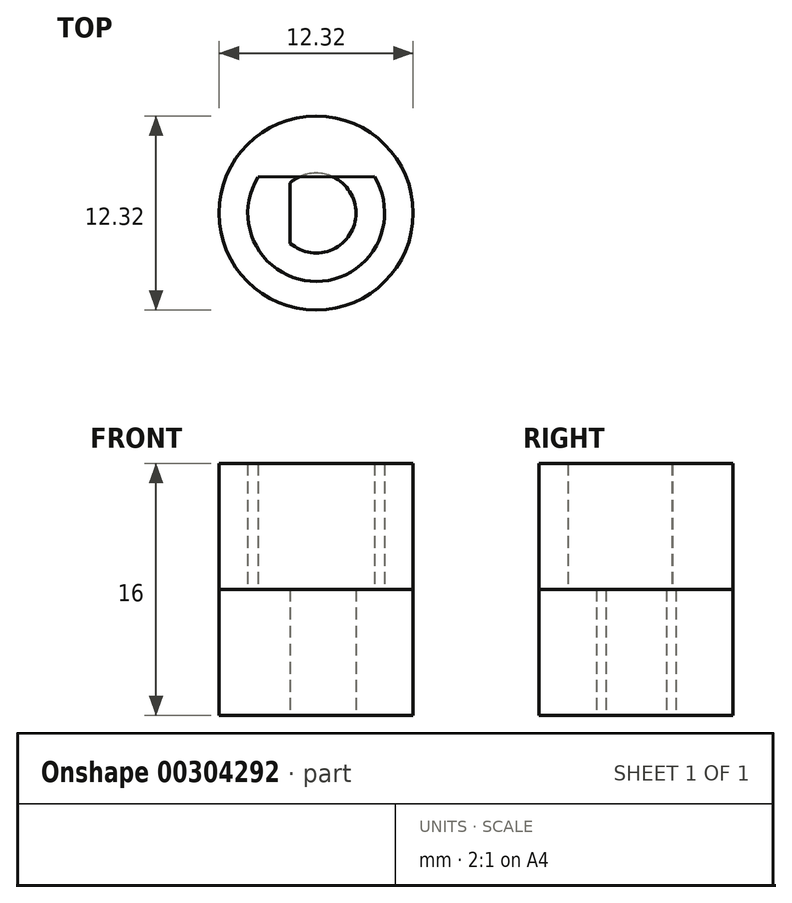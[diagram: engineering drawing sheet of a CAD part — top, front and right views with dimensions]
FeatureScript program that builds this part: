
annotation { "Feature Type Name" : "Feature", "Feature Type Description" : "" }
export const myFeature = defineFeature(function(context is Context, id is Id, definition is map)
    precondition{}
    {
        {
            var Q0;
            Q0=qCreatedBy(makeId("Top.planeOp"),FACE);
            var sketch = newSketch(context, id + "F0", { "sketchPlane" : qUnion([Q0])});
            skCircle(sketch, "E0", {"center": v(0, 0) * mm, "radius": 6.15 * mm});
            skArc(sketch, "E1.0", {"start": v(-1.65, -1.92) * mm, "mid": v(2.53, 0) * mm, "end": v(-1.65, 1.92) * mm});
            skLineSegment(sketch, "E2.0", {"start": v(-1.65, -1.92) * mm, "end": v(-1.65, 1.92) * mm});
            skSolve(sketch);
        }
        {
            var Q0;
            Q0=qCreatedBy(makeId("Top.planeOp"),FACE);
            cPlane(context, id + "F1", {"entities" : qUnion([Q0]), "cplaneType" : CPlaneType.OFFSET, "offset" : 8 * mm, "width" : 150 * mm, "height" : 150 * mm});
        }
        {
            var Q0;
            Q0=qCreatedBy(id+"F1.planeOp",FACE);
            var sketch = newSketch(context, id + "F2", { "sketchPlane" : qUnion([Q0])});
            skCircle(sketch, "E3", {"center": v(0, 0) * mm, "radius": 6.16 * mm});
            skArc(sketch, "E4.0", {"start": v(-3.7, 2.28) * mm, "mid": v(0.02, -4.34) * mm, "end": v(3.7, 2.3) * mm});
            skLineSegment(sketch, "E5", {"start": v(-3.7, 2.28) * mm, "end": v(3.7, 2.3) * mm});
            skSolve(sketch);
        }
        {
            var Q0;
            Q0=makeQuery(id+"F0.imprint","IMPRINT",FACE,{"disambiguationData":[TD([[makeQuery(id+"F0.imprint","IMPRINT",EDGE,{"derivedFrom":sQuery(id+"F0.wireOp",EDGE,"E0")}),1.0]])]});
            extrude(context, id + "F3", {"entities" : qUnion([Q0]), "depth" : 8 * mm});
        }
        {
            var Q0;
            Q0=makeQuery(id+"F2.imprint","IMPRINT",FACE,{"disambiguationData":[TD([[makeQuery(id+"F2.imprint","IMPRINT",EDGE,{"derivedFrom":sQuery(id+"F2.wireOp",EDGE,"E3")}),1.0]])]});
            extrude(context, id + "F4", {"entities" : qUnion([Q0]), "operationType" : NewBodyOperationType.ADD, "depth" : 8 * mm});
        }
    });
